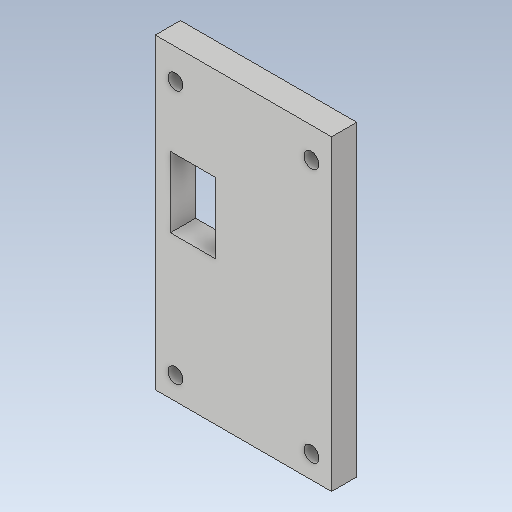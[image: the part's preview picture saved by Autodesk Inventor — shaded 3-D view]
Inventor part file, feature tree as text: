
AUTODESK INVENTOR PART (.ipt)
format: ipt  version: 2020.1 (Build 241239000, 239)  size: 134,144 bytes
history: native  units: mm
features: extrude x2, other x2, sketch x2
ambient origin geometry x8: Origin, YZ Plane, XZ Plane, XY Plane, X Axis, Y Axis, Z Axis, Center Point
bodies: Solid1 (feature_tree)
feature tree (6):
  extrude  "Extrusion1"  Depth=61.0mm
  extrude  "Extrusion2"  Depth=10.0mm
  other  "Edición directa1"
  sketch  "Sketch1"  dims[d0=38.0mm d1=61.0mm]
  sketch  "Sketch2"  dims[d2=4.0mm d3=6.0mm d4=4.0mm d5=6.0mm d6=4.0mm d7=4.5mm d8=4.0mm d9=4.5mm d10=3.0mm d11=3.0mm d12=3.0mm d13=3.0mm d14=5.0mm d15=0.0mm d16=3.0mm d17=18.5mm d18=9.0mm d19=14.0mm d20=9.0mm d21=10.0mm d22=0.0mm d23=0.0mm d24=0.0mm d25=-3.0mm]
  other  "Desplazar1"
